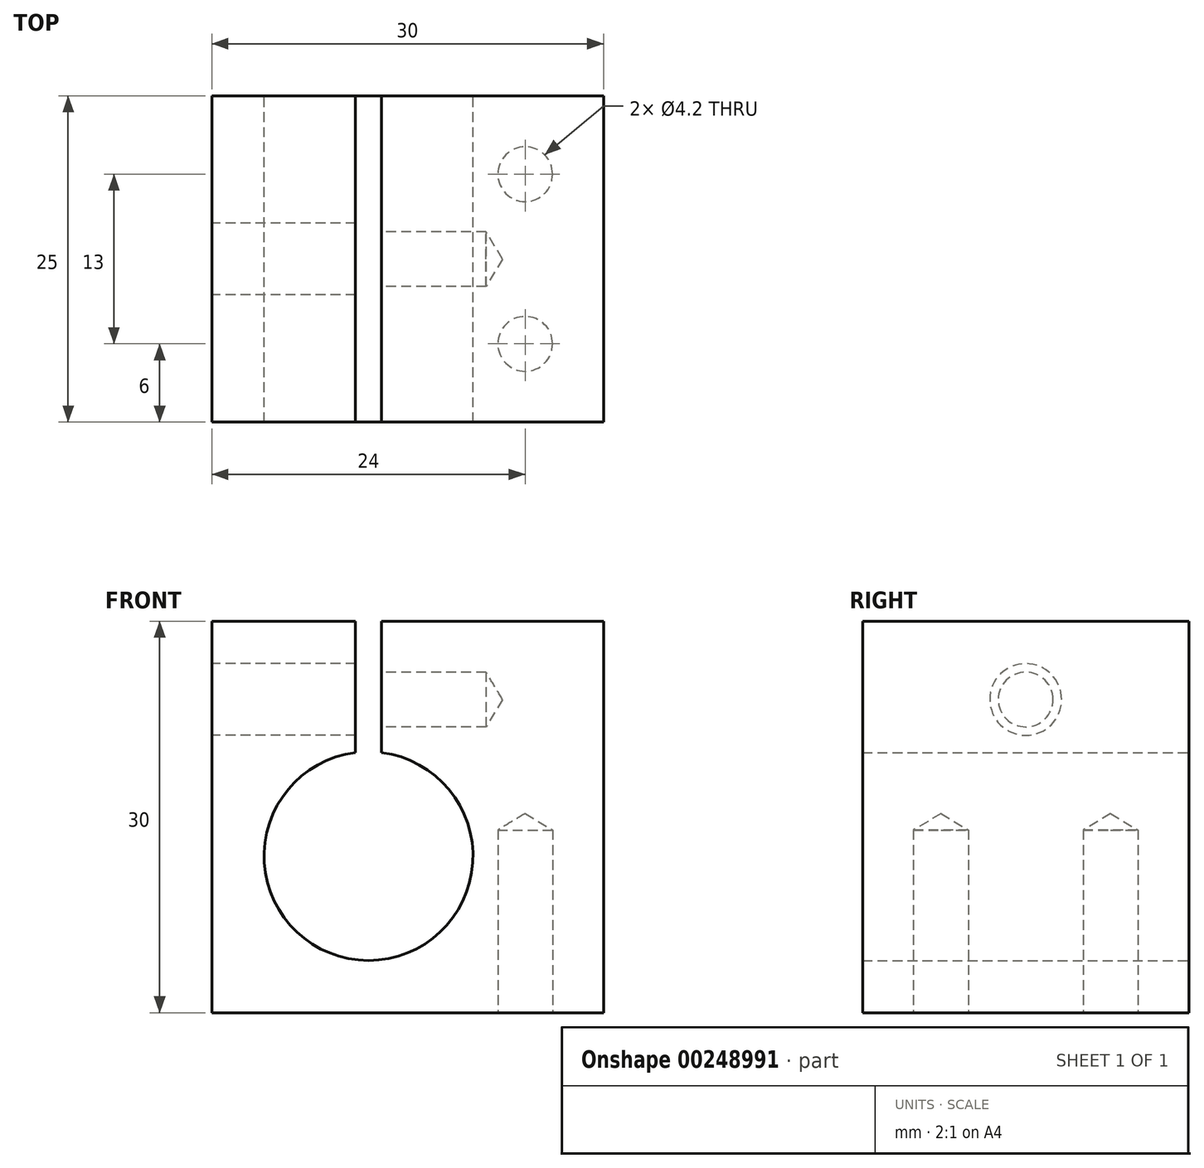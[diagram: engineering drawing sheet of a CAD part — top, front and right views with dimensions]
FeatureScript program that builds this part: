
annotation { "Feature Type Name" : "Feature", "Feature Type Description" : "" }
export const myFeature = defineFeature(function(context is Context, id is Id, definition is map)
    precondition{}
    {
        {
            var Q0;
            Q0=qCreatedBy(makeId("Front.planeOp"),FACE);
            var sketch = newSketch(context, id + "F0", { "sketchPlane" : qUnion([Q0])});
            skLineSegment(sketch, "E0.bottom", {"start": v(15, 15) * mm, "end": v(-2, 15) * mm});
            skLineSegment(sketch, "E0.top", {"start": v(15, -15) * mm, "end": v(-15, -15) * mm});
            skLineSegment(sketch, "E0.left", {"start": v(15, 15) * mm, "end": v(15, -15) * mm});
            skLineSegment(sketch, "E0.right", {"start": v(-15, 15) * mm, "end": v(-15, -15) * mm});
            skPoint(sketch, "E0.middle", {"position": v(0, 0) * mm});
            skArc(sketch, "E1", {"start": v(-4, 4.94) * mm, "mid": v(-3, -11) * mm, "end": v(-2, 4.94) * mm});
            skLineSegment(sketch, "E2.0", {"start": v(-2, 4.94) * mm, "end": v(-2, 15) * mm});
            skLineSegment(sketch, "E3.0", {"start": v(-4, 4.94) * mm, "end": v(-4, 15) * mm});
            skLineSegment(sketch, "E4.trimOffspring", {"start": v(-4, 15) * mm, "end": v(-15, 15) * mm});
            skSolve(sketch);
        }
        {
            var Q0;
            Q0=makeQuery(id+"F0.imprint","IMPRINT",FACE,{"disambiguationData":[TD([[makeQuery(id+"F0.imprint","IMPRINT",EDGE,{"derivedFrom":sQuery(id+"F0.wireOp",EDGE,"E0.bottom")}),1.0]])]});
            extrude(context, id + "F1", {"entities" : qUnion([Q0]), "endBound" : BoundingType.SYMMETRIC, "depth" : 25 * mm});
        }
        {
            var Q0;
            Q0=makeQuery(id+"F1.opExtrude","SWEPT_FACE",FACE,{"disambiguationData":[OSD([sQuery(id+"F0.wireOp",EDGE,"E0.right")])]});
            var sketch = newSketch(context, id + "F2", { "sketchPlane" : qUnion([Q0])});
            skPoint(sketch, "E5", {"position": v(0, 9) * mm});
            skSolve(sketch);
        }
        {
            var Q0;
            Q0=sQuery(id+"F2.wireOp",VERTEX,"E5");
            var Q1;
            Q1=makeQuery(id+"F1.opExtrude","SWEPT_BODY",BODY,{"disambiguationData":[OSD([sQuery(id+"F0.wireOp",EDGE,"E0.bottom"),sQuery(id+"F0.wireOp",EDGE,"E0.top"),sQuery(id+"F0.wireOp",EDGE,"E0.left"),sQuery(id+"F0.wireOp",EDGE,"E0.right"),sQuery(id+"F0.wireOp",EDGE,"E1"),sQuery(id+"F0.wireOp",EDGE,"E2.0"),sQuery(id+"F0.wireOp",EDGE,"E3.0"),sQuery(id+"F0.wireOp",EDGE,"E4.trimOffspring")])]});
            hole(context, id + "F3", {"style" : HoleStyle.SIMPLE, "endStyle" : HoleEndStyle.BLIND, "standardTappedOrClearance" : lookupTablePath({ "standard" : "ISO", "fit" : "Normal", "size" : "M5", "type" : "Clearance" }), "standardBlindInLast" : lookupTablePath({ "fit" : "Standard", "standard" : "ISO", "size" : "M5", "type" : "Clearance" }), "holeDiameter" : 5.5 * mm, "holeDepth" : 12 * mm, "tappedDepth" : 5.6 * mm, "tapClearance" : 3, "startFromSketch" : true, "locations" : qUnion([Q0]), "scope" : qUnion([Q1])});
        }
        {
            var Q0;
            Q0=makeQuery(id+"F1.opExtrude","SWEPT_FACE",FACE,{"disambiguationData":[OSD([sQuery(id+"F0.wireOp",EDGE,"E2.0")])]});
            var sketch = newSketch(context, id + "F4", { "sketchPlane" : qUnion([Q0])});
            skPoint(sketch, "E6", {"position": v(0, 9) * mm});
            skSolve(sketch);
        }
        {
            var Q0;
            Q0=sQuery(id+"F4.wireOp",VERTEX,"E6");
            var Q1;
            Q1=makeQuery(id+"F1.opExtrude","SWEPT_BODY",BODY,{"disambiguationData":[OSD([sQuery(id+"F0.wireOp",EDGE,"E0.bottom"),sQuery(id+"F0.wireOp",EDGE,"E0.top"),sQuery(id+"F0.wireOp",EDGE,"E0.left"),sQuery(id+"F0.wireOp",EDGE,"E0.right"),sQuery(id+"F0.wireOp",EDGE,"E1"),sQuery(id+"F0.wireOp",EDGE,"E2.0"),sQuery(id+"F0.wireOp",EDGE,"E3.0"),sQuery(id+"F0.wireOp",EDGE,"E4.trimOffspring")])]});
            hole(context, id + "F5", {"style" : HoleStyle.SIMPLE, "endStyle" : HoleEndStyle.BLIND, "standardTappedOrClearance" : lookupTablePath({ "standard" : "ISO", "engagement" : "75%", "pitch" : "0.8 mm", "size" : "M5", "type" : "Tapped" }), "standardBlindInLast" : lookupTablePath({ "standard" : "ISO", "engagement" : "75%", "pitch" : "0.8 mm", "size" : "M5", "type" : "Tapped" }), "holeDiameter" : 4.2 * mm, "showTappedDepth" : true, "holeDepth" : 8 * mm, "tappedDepth" : 5.6 * mm, "tapClearance" : 3, "startFromSketch" : true, "locations" : qUnion([Q0]), "scope" : qUnion([Q1]), "majorDiameter" : 5 * mm});
        }
        {
            var Q0;
            Q0=makeQuery(id+"F1.opExtrude","SWEPT_FACE",FACE,{"disambiguationData":[OSD([sQuery(id+"F0.wireOp",EDGE,"E0.top")])]});
            var sketch = newSketch(context, id + "F6", { "sketchPlane" : qUnion([Q0])});
            skPoint(sketch, "E7", {"position": v(9, 6.5) * mm});
            skPoint(sketch, "E8", {"position": v(9, -6.5) * mm});
            skSolve(sketch);
        }
        {
            var Q0;
            Q0=sQuery(id+"F6.wireOp",VERTEX,"E7");
            var Q1;
            Q1=sQuery(id+"F6.wireOp",VERTEX,"E8");
            var Q2;
            Q2=makeQuery(id+"F1.opExtrude","SWEPT_BODY",BODY,{"disambiguationData":[OSD([sQuery(id+"F0.wireOp",EDGE,"E0.bottom"),sQuery(id+"F0.wireOp",EDGE,"E0.top"),sQuery(id+"F0.wireOp",EDGE,"E0.left"),sQuery(id+"F0.wireOp",EDGE,"E0.right"),sQuery(id+"F0.wireOp",EDGE,"E1"),sQuery(id+"F0.wireOp",EDGE,"E2.0"),sQuery(id+"F0.wireOp",EDGE,"E3.0"),sQuery(id+"F0.wireOp",EDGE,"E4.trimOffspring")])]});
            hole(context, id + "F7", {"style" : HoleStyle.SIMPLE, "endStyle" : HoleEndStyle.BLIND, "standardTappedOrClearance" : lookupTablePath({ "standard" : "ISO", "engagement" : "75%", "pitch" : "0.8 mm", "size" : "M5", "type" : "Tapped" }), "standardBlindInLast" : lookupTablePath({ "standard" : "ISO", "engagement" : "75%", "pitch" : "0.8 mm", "size" : "M5", "type" : "Tapped" }), "holeDiameter" : 4.2 * mm, "showTappedDepth" : true, "holeDepth" : 14 * mm, "tappedDepth" : 11.6 * mm, "tapClearance" : 3, "startFromSketch" : true, "locations" : qUnion([Q0, Q1]), "scope" : qUnion([Q2]), "majorDiameter" : 5 * mm});
        }
    });
